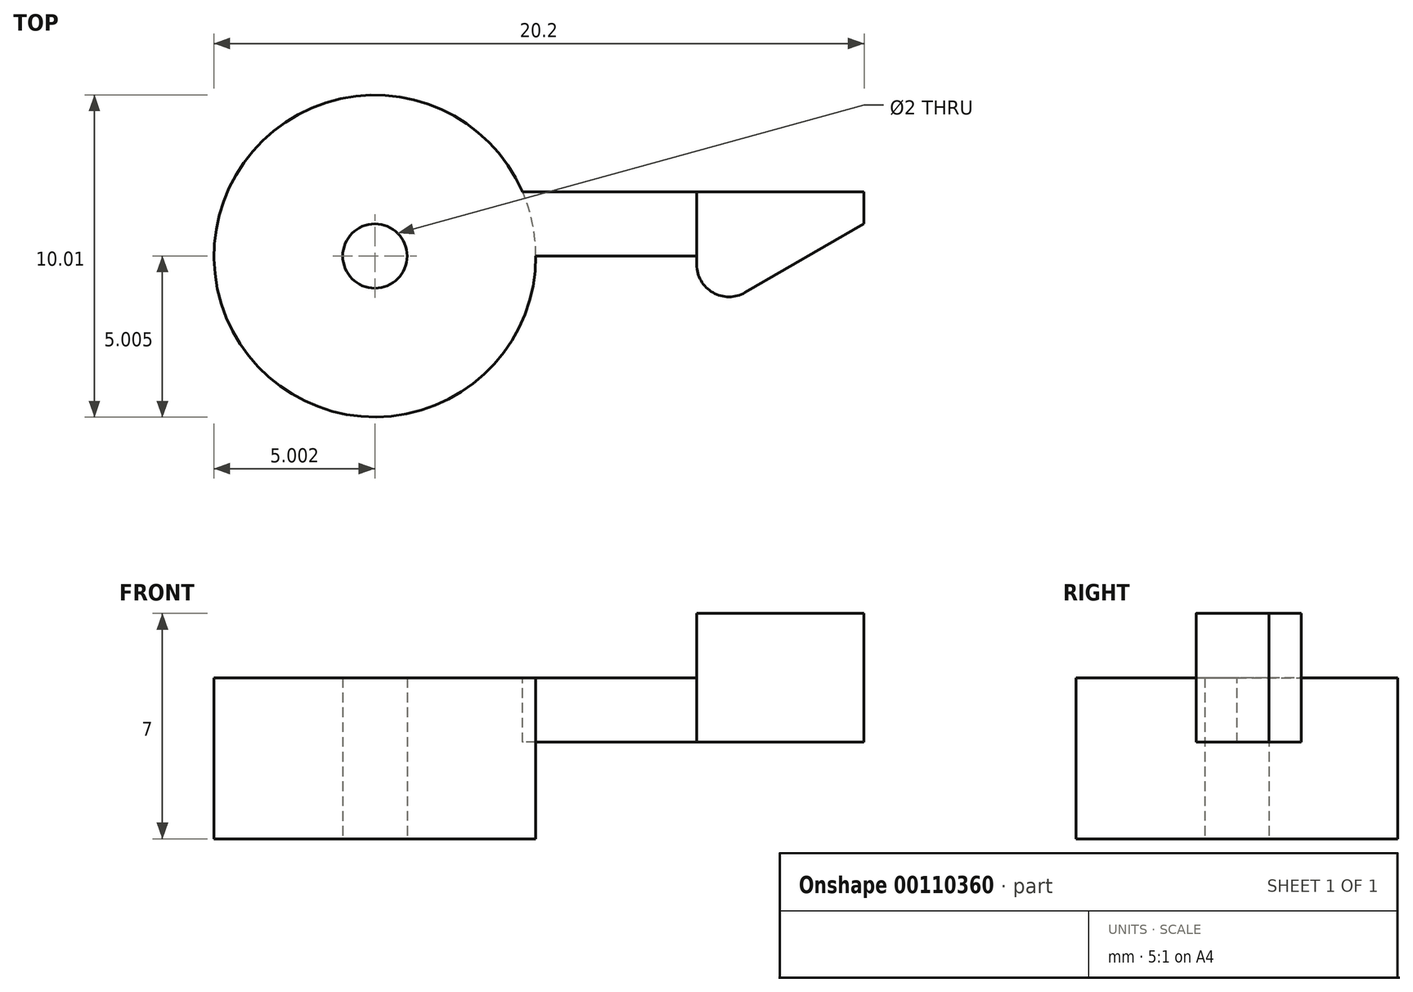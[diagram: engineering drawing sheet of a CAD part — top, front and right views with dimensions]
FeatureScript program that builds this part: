
annotation { "Feature Type Name" : "Feature", "Feature Type Description" : "" }
export const myFeature = defineFeature(function(context is Context, id is Id, definition is map)
    precondition{}
    {
        {
            var Q0;
            Q0=qCreatedBy(makeId("Top.planeOp"),FACE);
            var sketch = newSketch(context, id + "F0", { "sketchPlane" : qUnion([Q0])});
            skCircle(sketch, "E0", {"center": v(-9.4, -1.13) * mm, "radius": 5 * mm});
            skLineSegment(sketch, "E1", {"start": v(-4.4, -1.13) * mm, "end": v(0.6, -1.13) * mm});
            skLineSegment(sketch, "E2", {"start": v(0.6, -1.13) * mm, "end": v(0.6, 0.88) * mm});
            skLineSegment(sketch, "E3", {"start": v(0.6, 0.88) * mm, "end": v(-4.82, 0.87) * mm});
            skLineSegment(sketch, "E4", {"start": v(0.6, 0.88) * mm, "end": v(5.8, 0.88) * mm});
            skLineSegment(sketch, "E5", {"start": v(5.8, 0.88) * mm, "end": v(5.8, -0.12) * mm});
            skLineSegment(sketch, "E6", {"start": v(0.6, -1.13) * mm, "end": v(0.6, -3.12) * mm});
            skLineSegment(sketch, "E7", {"start": v(0.6, -3.12) * mm, "end": v(5.8, -0.13) * mm});
            skLineSegment(sketch, "E8", {"start": v(0.6, 0.88) * mm, "end": v(0.6, -1.13) * mm});
            skSolve(sketch);
        }
        {
            var Q0;
            {var subQ0=sQuery(id+"F0.wireOp",EDGE,"E1");Q0=makeQuery(id+"F0.imprint","IMPRINT",FACE,{"disambiguationData":[TD([[makeQuery(id+"F0.imprint","IMPRINT",EDGE,{"derivedFrom":subQ0}),1.0]])]});}
            extrude(context, id + "F1", {"entities" : qUnion([Q0]), "oppositeDirection" : true, "depth" : 2 * mm});
        }
        {
            var Q0;
            Q0=makeQuery(id+"F0.imprint","IMPRINT",FACE,{"disambiguationData":[TD([[makeQuery(id+"F0.imprint","IMPRINT",EDGE,{"derivedFrom":sQuery(id+"F0.wireOp",EDGE,"E4")}),-1.0]])]});
            extrude(context, id + "F2", {"entities" : qUnion([Q0]), "operationType" : NewBodyOperationType.ADD, "depth" : 4 * mm, "symmetric" : true});
        }
        {
            var Q0;
            {var subQ0=sQuery(id+"F0.wireOp",EDGE,"E0");var subQ1=makeQuery(id+"F0.imprint","INTERSECT",VERTEX,{"derivedFrom":[subQ0,sQuery(id+"F0.wireOp",EDGE,"E1")]});Q0=makeQuery(id+"F0.imprint","IMPRINT",FACE,{"disambiguationData":[TD([[makeQuery(id+"F0.imprint","IMPRINT",EDGE,{"disambiguationData":[TD([[subQ1,-1.0]])],"derivedFrom":subQ0}),1.0]])]});}
            extrude(context, id + "F3", {"entities" : qUnion([Q0]), "operationType" : NewBodyOperationType.ADD, "oppositeDirection" : true, "depth" : 5 * mm});
        }
        {
            var Q0;
            Q0=makeQuery(id+"F2.opExtrude","SWEPT_EDGE",EDGE,{"disambiguationData":[OSD([sQuery(id+"F0.wireOp",EDGE,"E6"),sQuery(id+"F0.wireOp",EDGE,"E7")])]});
            fillet(context, id + "F4", {"entities" : qUnion([Q0]), "radius" : 1 * mm, "tangentPropagation" : true, "allowEdgeOverflow" : false});
        }
        {
            var Q0;
            Q0=sQuery(id+"F0.wireOp",VERTEX,"E0.center");
            var Q1;
            Q1=makeQuery(id+"F1.opExtrude","SWEPT_BODY",BODY,{"disambiguationData":[OSD([sQuery(id+"F0.wireOp",EDGE,"E0"),sQuery(id+"F0.wireOp",EDGE,"E1"),sQuery(id+"F0.wireOp",EDGE,"E3"),sQuery(id+"F0.wireOp",EDGE,"E8")])]});
            hole(context, id + "F5", {"style" : HoleStyle.SIMPLE, "endStyle" : HoleEndStyle.THROUGH, "holeDiameter" : 2 * mm, "locations" : qUnion([Q0]), "scope" : qUnion([Q1]), "isTappedThrough" : true});
        }
    });
